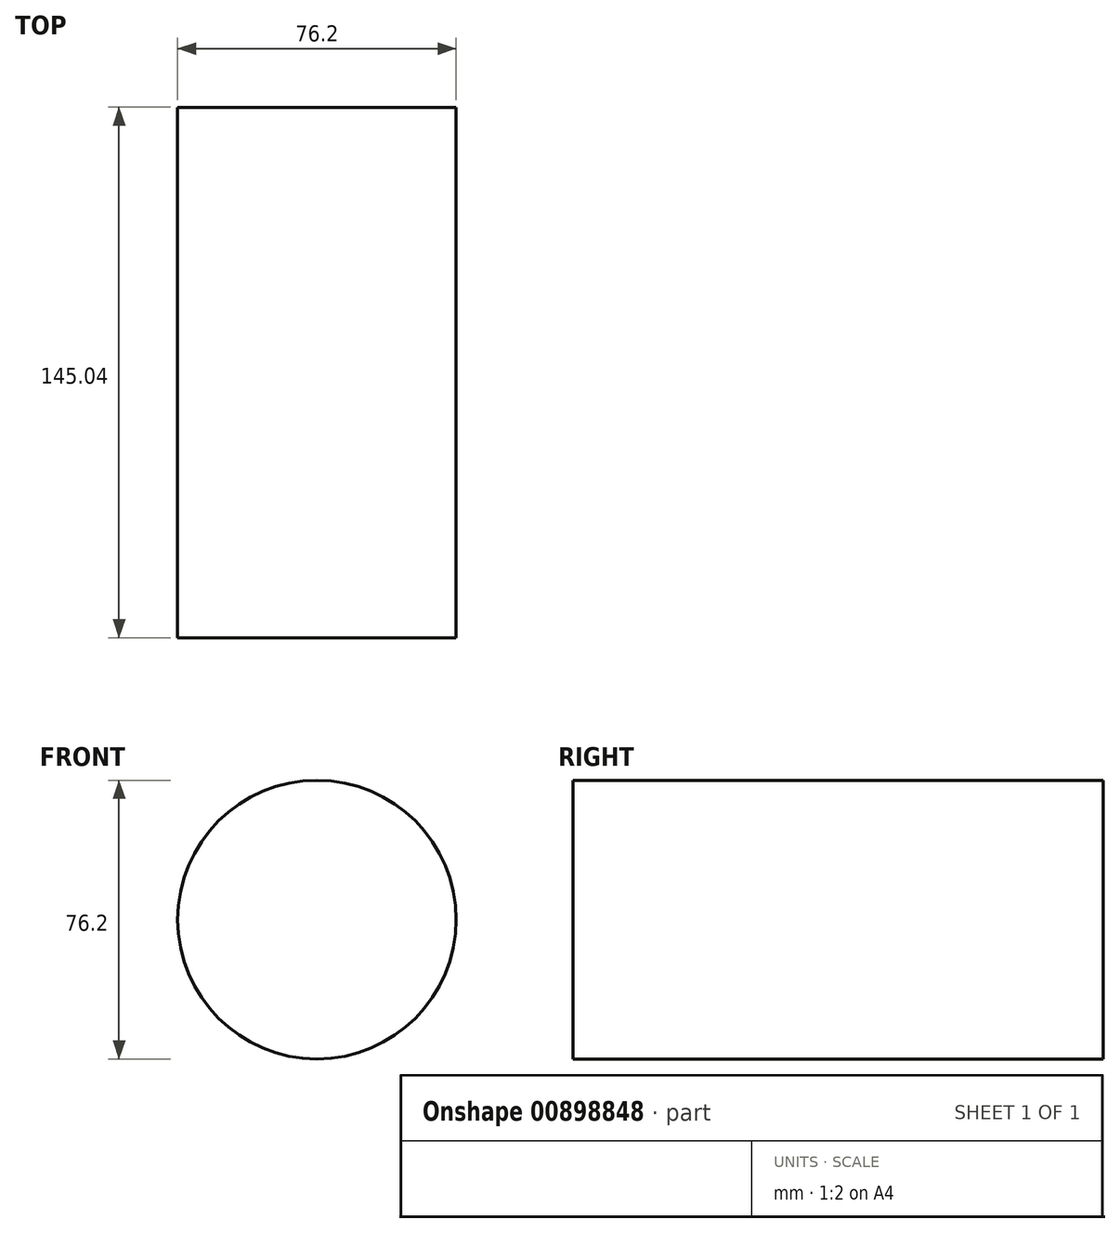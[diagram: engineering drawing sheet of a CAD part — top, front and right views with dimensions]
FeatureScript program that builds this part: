
annotation { "Feature Type Name" : "Feature", "Feature Type Description" : "" }
export const myFeature = defineFeature(function(context is Context, id is Id, definition is map)
    precondition{}
    {
        {
            var Q0;
            Q0=qCreatedBy(makeId("Front.planeOp"),FACE);
            var sketch = newSketch(context, id + "F0", { "sketchPlane" : qUnion([Q0])});
            skCircle(sketch, "E0", {"center": v(0, 0) * mm, "radius": 38.1 * mm});
            skSolve(sketch);
        }
        {
            var Q0;
            Q0 = qSketchRegion(id + "F0", true);
            extrude(context, id + "F1", {"entities" : qUnion([Q0]), "endBound" : BoundingType.SYMMETRIC, "depth" : 145.03 * mm, "hasOffset" : true, "offsetDistance" : 127 * mm});
        }
    });
